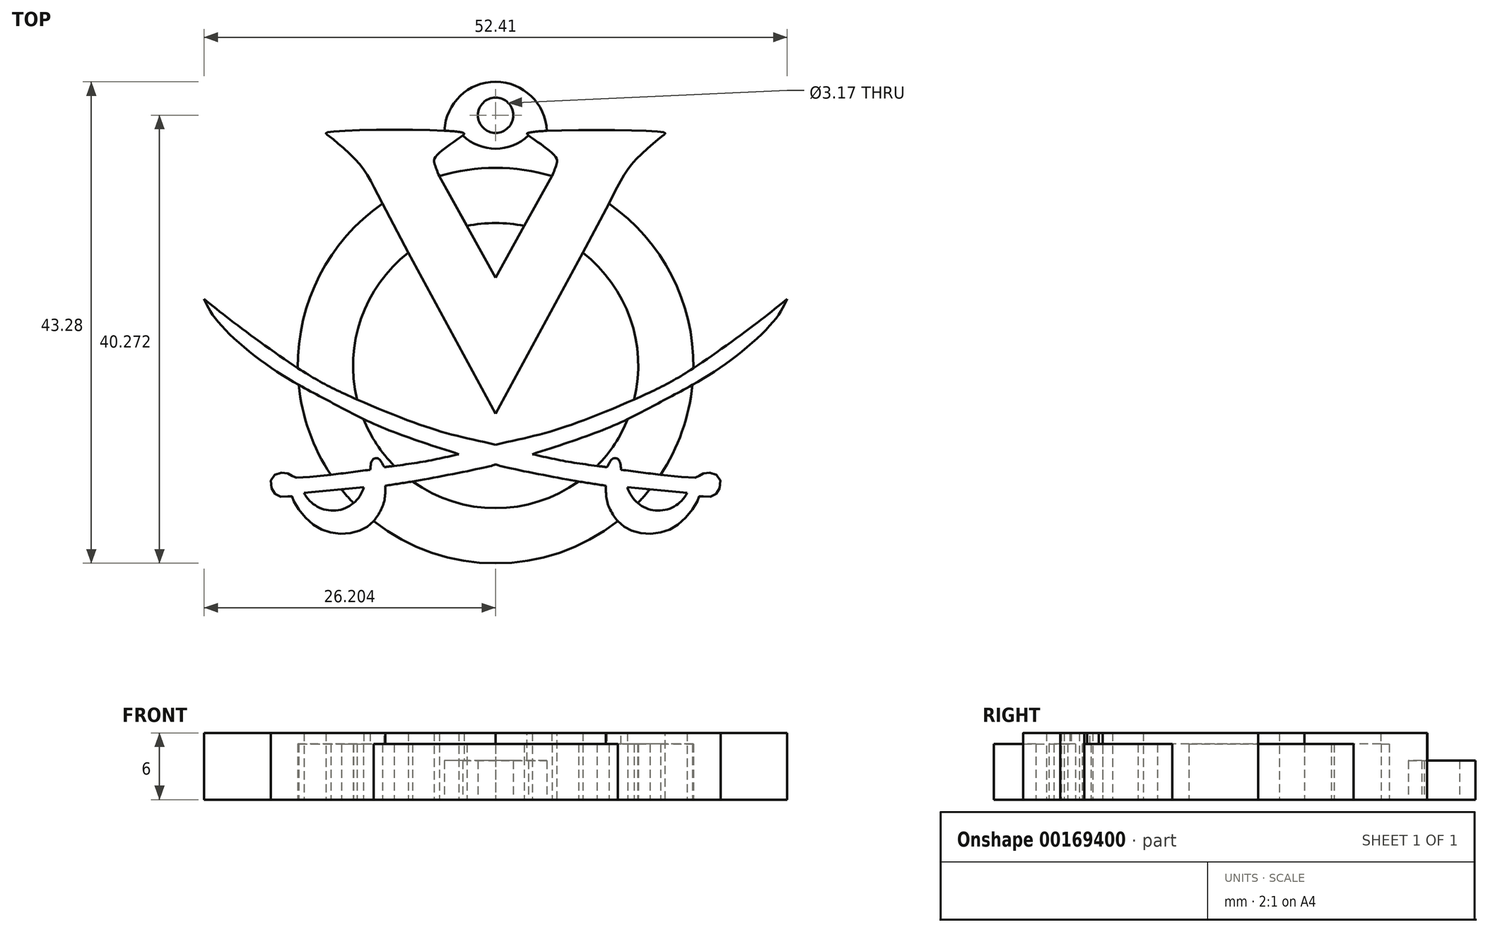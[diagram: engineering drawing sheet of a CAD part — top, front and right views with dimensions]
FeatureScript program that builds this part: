
annotation { "Feature Type Name" : "Feature", "Feature Type Description" : "" }
export const myFeature = defineFeature(function(context is Context, id is Id, definition is map)
    precondition{}
    {
        {
            var Q0;
            Q0=qCreatedBy(makeId("Top.planeOp"),FACE);
            var sketch = newSketch(context, id + "F0", { "sketchPlane" : qUnion([Q0])});
            skFitSpline(sketch, "E0", {"points": [v(-5.25, 12.26) * mm, v(-5.62, 13.2) * mm, v(-5.62, 14) * mm, v(-3.16, 15.95) * mm, v(-3.1, 16.18) * mm, v(-15.31, 16.24) * mm, v(-15.46, 16.13) * mm, v(-15.03, 15.78) * mm, v(-12.5, 13.45) * mm, v(-10.71, 10.47) * mm, v(-0.2, -9.06) * mm], "startDerivative": vector(-7.95, 17.65) * mm, "endDerivative": vector(52.14, -95.86) * mm});
            skFitSpline(sketch, "E1", {"points": [v(-26.41, 1.25) * mm, v(-23.23, -1.23) * mm, v(-17.64, -5.17) * mm, v(-13.77, -7.28) * mm, v(-7.6, -9.83) * mm, v(-3.93, -10.98) * mm, v(-0.2, -11.84) * mm], "startDerivative": vector(18.76, -15.03) * mm, "endDerivative": vector(25.87, -5.68) * mm});
            skFitSpline(sketch, "E2", {"points": [v(-26.41, 1.25) * mm, v(-25.22, -0.7) * mm, v(-20.44, -4.89) * mm, v(-15.23, -7.9) * mm, v(-10.64, -10.2) * mm, v(-3.5, -12.7) * mm], "startDerivative": vector(6.64, -13.77) * mm, "endDerivative": vector(31.84, -10.2) * mm});
            skFitSpline(sketch, "E3", {"points": [v(-3.5, -12.7) * mm, v(-6.8, -13.39) * mm, v(-10.22, -13.86) * mm], "startDerivative": vector(-6.6, -1.5) * mm, "endDerivative": vector(-6.83, -0.83) * mm});
            skFitSpline(sketch, "E4", {"points": [v(-10.22, -13.86) * mm, v(-10.4, -13.52) * mm, v(-10.77, -13.08) * mm, v(-11.25, -13.18) * mm, v(-11.47, -14.1) * mm], "startDerivative": vector(-0.83, 1.52) * mm, "endDerivative": vector(-0.23, -3.43) * mm});
            skFitSpline(sketch, "E5", {"points": [v(-11.47, -14.1) * mm, v(-18.34, -14.77) * mm, v(-18.5, -14.65) * mm, v(-18.87, -14.43) * mm, v(-19.6, -14.38) * mm, v(-20.3, -14.79) * mm, v(-20.34, -15.75) * mm, v(-19.91, -16.34) * mm, v(-19.15, -16.53) * mm, v(-18.55, -16.43) * mm, v(-18.48, -16.58) * mm, v(-17.97, -17.56) * mm, v(-16.65, -18.96) * mm, v(-15.25, -19.67) * mm, v(-13.56, -19.82) * mm, v(-12.1, -19.42) * mm, v(-11.11, -18.64) * mm, v(-10.25, -17.04) * mm, v(-10.12, -15.53) * mm], "startDerivative": vector(-70.38, -9.26) * mm, "endDerivative": vector(-0.27, 23.36) * mm});
            skLineSegment(sketch, "E6", {"start": v(-17.42, -16.18) * mm, "end": v(-12.05, -15.67) * mm});
            skArc(sketch, "E7", {"start": v(-17.42, -16.18) * mm, "mid": v(-14.56, -17.76) * mm, "end": v(-12.05, -15.67) * mm});
            skFitSpline(sketch, "E8", {"points": [v(-10.12, -15.53) * mm, v(-6.27, -14.9) * mm, v(-0.62, -13.75) * mm, v(-0.2, -13.62) * mm], "startDerivative": vector(8.45, 1.27) * mm, "endDerivative": vector(2.06, 0.83) * mm});
            skFitSpline(sketch, "E9.MirrorCS", {"points": [v(4.85, 12.27) * mm, v(5.21, 13.2) * mm, v(5.2, 14) * mm, v(2.75, 15.96) * mm, v(2.7, 16.18) * mm, v(14.9, 16.23) * mm, v(15.03, 16.13) * mm, v(14.62, 15.78) * mm, v(12.1, 13.45) * mm, v(10.3, 10.47) * mm, v(-0.2, -9.05) * mm], "startDerivative": vector(7.95, 17.65) * mm, "endDerivative": vector(-52.14, -95.86) * mm});
            skFitSpline(sketch, "E10.MirrorCS", {"points": [v(26, 1.25) * mm, v(22.82, -1.23) * mm, v(17.23, -5.17) * mm, v(13.36, -7.28) * mm, v(7.2, -9.83) * mm, v(3.52, -10.98) * mm, v(-0.2, -11.84) * mm], "startDerivative": vector(-18.76, -15.03) * mm, "endDerivative": vector(-25.87, -5.68) * mm});
            skFitSpline(sketch, "E11.MirrorCS", {"points": [v(26, 1.25) * mm, v(24.8, -0.7) * mm, v(20.03, -4.89) * mm, v(14.82, -7.9) * mm, v(10.23, -10.2) * mm, v(3.09, -12.7) * mm], "startDerivative": vector(-6.64, -13.77) * mm, "endDerivative": vector(-31.84, -10.2) * mm});
            skFitSpline(sketch, "E12.MirrorCS", {"points": [v(3.09, -12.7) * mm, v(6.4, -13.39) * mm, v(9.8, -13.86) * mm], "startDerivative": vector(6.6, -1.5) * mm, "endDerivative": vector(6.83, -0.83) * mm});
            skFitSpline(sketch, "E13.MirrorCS", {"points": [v(9.8, -13.86) * mm, v(10, -13.52) * mm, v(10.36, -13.08) * mm, v(10.84, -13.18) * mm, v(11.06, -14.1) * mm], "startDerivative": vector(0.83, 1.52) * mm, "endDerivative": vector(0.23, -3.43) * mm});
            skFitSpline(sketch, "E14.MirrorCS", {"points": [v(11.06, -14.1) * mm, v(17.93, -14.77) * mm, v(18.08, -14.65) * mm, v(18.46, -14.43) * mm, v(19.18, -14.38) * mm, v(19.9, -14.79) * mm, v(19.93, -15.75) * mm, v(19.5, -16.34) * mm, v(18.74, -16.53) * mm, v(18.13, -16.43) * mm, v(18.07, -16.58) * mm, v(17.56, -17.56) * mm, v(16.24, -18.96) * mm, v(14.84, -19.67) * mm, v(13.15, -19.82) * mm, v(11.68, -19.42) * mm, v(10.7, -18.64) * mm, v(9.84, -17.04) * mm, v(9.7, -15.53) * mm], "startDerivative": vector(70.38, -9.26) * mm, "endDerivative": vector(0.27, 23.36) * mm});
            skLineSegment(sketch, "E15.MirrorCS", {"start": v(17, -16.18) * mm, "end": v(11.64, -15.67) * mm});
            skFitSpline(sketch, "E16.MirrorCS", {"points": [v(9.7, -15.53) * mm, v(5.85, -14.9) * mm, v(0.21, -13.75) * mm, v(-0.2, -13.62) * mm], "startDerivative": vector(-8.45, 1.27) * mm, "endDerivative": vector(-2.06, 0.83) * mm});
            skArc(sketch, "E17.MirrorCS", {"start": v(17, -16.18) * mm, "mid": v(14.15, -17.76) * mm, "end": v(11.64, -15.67) * mm});
            skArc(sketch, "E18", {"start": v(-8.04, 5.4) * mm, "mid": v(-12.3, -0.5) * mm, "end": v(-12.65, -7.78) * mm});
            skArc(sketch, "E19", {"start": v(-10.38, 9.83) * mm, "mid": v(-16.02, 3.38) * mm, "end": v(-17.97, -4.96) * mm});
            skArc(sketch, "E20", {"start": v(-3.16, 15.95) * mm, "mid": v(-0.2, 14.76) * mm, "end": v(2.75, 15.96) * mm});
            skCircle(sketch, "E21", {"center": v(-0.2, 17.77) * mm, "radius": 1.59 * mm});
            skArc(sketch, "E22.trimOffspring", {"start": v(4.86, 12.3) * mm, "mid": v(-0.2, 13.04) * mm, "end": v(-5.27, 12.3) * mm});
            skArc(sketch, "E23.trimOffspring", {"start": v(2.38, 7.82) * mm, "mid": v(-0.2, 8.08) * mm, "end": v(-2.79, 7.82) * mm});
            skArc(sketch, "E24.trimOffspring", {"start": v(12.24, -7.78) * mm, "mid": v(11.9, -0.5) * mm, "end": v(7.63, 5.4) * mm});
            skArc(sketch, "E25.trimOffspring", {"start": v(17.56, -4.96) * mm, "mid": v(15.6, 3.38) * mm, "end": v(9.97, 9.83) * mm});
            skArc(sketch, "E26.trimOffspring", {"start": v(-12.09, -9.53) * mm, "mid": v(-10.9, -11.78) * mm, "end": v(-9.31, -13.75) * mm});
            skArc(sketch, "E27.trimOffspring", {"start": v(-17.9, -6.46) * mm, "mid": v(-16.95, -10.68) * mm, "end": v(-15.02, -14.55) * mm});
            skArc(sketch, "E28.trimOffspring", {"start": v(-14.06, -15.86) * mm, "mid": v(-13.53, -16.49) * mm, "end": v(-12.97, -17.1) * mm});
            skArc(sketch, "E29.trimOffspring", {"start": v(-11.17, -18.71) * mm, "mid": v(-0.2, -22.5) * mm, "end": v(10.76, -18.71) * mm});
            skArc(sketch, "E30.trimOffspring", {"start": v(12.56, -17.1) * mm, "mid": v(13.12, -16.49) * mm, "end": v(13.65, -15.86) * mm});
            skArc(sketch, "E31.trimOffspring", {"start": v(14.6, -14.55) * mm, "mid": v(16.54, -10.68) * mm, "end": v(17.48, -6.46) * mm});
            skArc(sketch, "E32.trimOffspring", {"start": v(-7.67, -15.15) * mm, "mid": v(-0.2, -17.55) * mm, "end": v(7.26, -15.15) * mm});
            skArc(sketch, "E33.trimOffspring", {"start": v(8.9, -13.75) * mm, "mid": v(10.5, -11.78) * mm, "end": v(11.68, -9.53) * mm});
            skArc(sketch, "E34", {"start": v(4.4, 16.37) * mm, "mid": v(-0.2, 20.78) * mm, "end": v(-4.8, 16.38) * mm});
            skLineSegment(sketch, "E35", {"start": v(-5.25, 12.26) * mm, "end": v(-2.79, 7.82) * mm});
            skLineSegment(sketch, "E36", {"start": v(-2.79, 7.82) * mm, "end": v(-0.2, 3.17) * mm});
            skLineSegment(sketch, "E37", {"start": v(4.85, 12.27) * mm, "end": v(2.38, 7.82) * mm});
            skLineSegment(sketch, "E38", {"start": v(-0.2, 3.17) * mm, "end": v(2.38, 7.82) * mm});
            skLineSegment(sketch, "E39", {"start": v(-10.38, 9.83) * mm, "end": v(-8.04, 5.4) * mm});
            skLineSegment(sketch, "E40", {"start": v(9.97, 9.83) * mm, "end": v(7.63, 5.4) * mm});
            skLineSegment(sketch, "E41", {"start": v(7.63, 5.4) * mm, "end": v(-0.2, -9.05) * mm});
            skLineSegment(sketch, "E42", {"start": v(-0.2, -9.05) * mm, "end": v(-8.04, 5.4) * mm});
            skSolve(sketch);
        }
        {
            var Q0;
            {var subQ0=sQuery(id+"F0.wireOp",EDGE,"0hUFmzZZ-p1u1-aZ5k-ukOv-5giL6xZqdYDg");Q0=makeQuery(id+"F0.imprint","IMPRINT",FACE,{"disambiguationData":[TD([[makeQuery(id+"F0.imprint","IMPRINT",EDGE,{"derivedFrom":subQ0}),1.0]])]});}
            var Q1;
            {var subQ37=sQuery(id+"F0.wireOp",EDGE,"E4");Q1=makeQuery(id+"F0.imprint","IMPRINT",FACE,{"disambiguationData":[TD([[makeQuery(id+"F0.imprint","IMPRINT",EDGE,{"derivedFrom":subQ37}),1.0]])]});}
            var Q2;
            {var subQ0=sQuery(id+"F0.wireOp",EDGE,"E35");Q2=makeQuery(id+"F0.imprint","IMPRINT",FACE,{"disambiguationData":[TD([[makeQuery(id+"F0.imprint","IMPRINT",EDGE,{"derivedFrom":subQ0}),-1.0]])]});}
            extrude(context, id + "F1", {"entities" : qUnion([Q0, Q1, Q2]), "depth" : 6 * mm, "offsetDistance" : 25 * mm});
        }
        {
            var Q0;
            {var subQ0=sQuery(id+"F0.wireOp",EDGE,"E22.trimOffspring");Q0=makeQuery(id+"F0.imprint","IMPRINT",FACE,{"disambiguationData":[TD([[makeQuery(id+"F0.imprint","IMPRINT",EDGE,{"derivedFrom":subQ0}),1.0]])]});}
            var Q1;
            {var subQ0=sQuery(id+"F0.wireOp",EDGE,"E24.trimOffspring");Q1=makeQuery(id+"F0.imprint","IMPRINT",FACE,{"disambiguationData":[TD([[makeQuery(id+"F0.imprint","IMPRINT",EDGE,{"derivedFrom":subQ0}),-1.0]])]});}
            var Q2;
            {var subQ0=sQuery(id+"F0.wireOp",EDGE,"E13.MirrorCS");Q2=makeQuery(id+"F0.imprint","IMPRINT",FACE,{"disambiguationData":[TD([[makeQuery(id+"F0.imprint","IMPRINT",EDGE,{"derivedFrom":subQ0}),1.0]])]});}
            var Q3;
            {var subQ7=sQuery(id+"F0.wireOp",EDGE,"E29.trimOffspring");Q3=makeQuery(id+"F0.imprint","IMPRINT",FACE,{"disambiguationData":[TD([[makeQuery(id+"F0.imprint","IMPRINT",EDGE,{"derivedFrom":subQ7}),1.0]])]});}
            var Q4;
            {var subQ0=sQuery(id+"F0.wireOp",EDGE,"E4");Q4=makeQuery(id+"F0.imprint","IMPRINT",FACE,{"disambiguationData":[TD([[makeQuery(id+"F0.imprint","IMPRINT",EDGE,{"derivedFrom":subQ0}),-1.0]])]});}
            var Q5;
            {var subQ3=sQuery(id+"F0.wireOp",EDGE,"E28.trimOffspring");Q5=makeQuery(id+"F0.imprint","IMPRINT",FACE,{"disambiguationData":[TD([[makeQuery(id+"F0.imprint","IMPRINT",EDGE,{"derivedFrom":subQ3}),1.0]])]});}
            var Q6;
            {var subQ3=sQuery(id+"F0.wireOp",EDGE,"E30.trimOffspring");Q6=makeQuery(id+"F0.imprint","IMPRINT",FACE,{"disambiguationData":[TD([[makeQuery(id+"F0.imprint","IMPRINT",EDGE,{"derivedFrom":subQ3}),1.0]])]});}
            var Q7;
            {var subQ0=sQuery(id+"F0.wireOp",EDGE,"E18");Q7=makeQuery(id+"F0.imprint","IMPRINT",FACE,{"disambiguationData":[TD([[makeQuery(id+"F0.imprint","IMPRINT",EDGE,{"derivedFrom":subQ0}),-1.0]])]});}
            extrude(context, id + "F2", {"entities" : qUnion([Q0, Q1, Q2, Q3, Q4, Q5, Q6, Q7]), "operationType" : NewBodyOperationType.ADD, "depth" : 5 * mm, "offsetDistance" : 25 * mm});
        }
        {
            var Q0;
            {var subQ0=sQuery(id+"F0.wireOp",EDGE,"E20");Q0=makeQuery(id+"F0.imprint","IMPRINT",FACE,{"disambiguationData":[TD([[makeQuery(id+"F0.imprint","IMPRINT",EDGE,{"derivedFrom":subQ0}),1.0]])]});}
            extrude(context, id + "F3", {"entities" : qUnion([Q0]), "operationType" : NewBodyOperationType.ADD, "depth" : 3.5 * mm, "offsetDistance" : 25 * mm});
        }
    });
